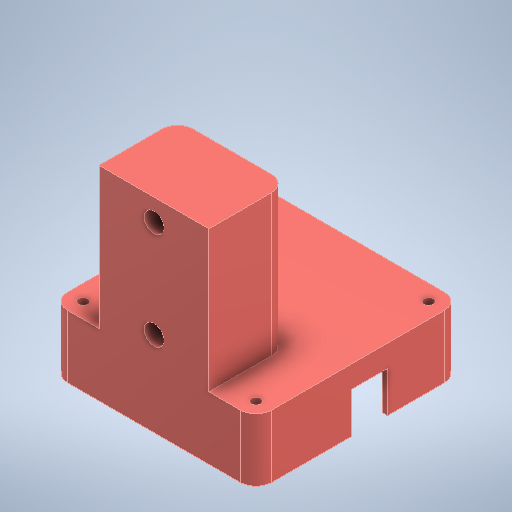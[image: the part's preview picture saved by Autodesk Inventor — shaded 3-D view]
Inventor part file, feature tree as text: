
AUTODESK INVENTOR PART (.ipt)
format: ipt  version: 2025.2 (Build 292293000, 293)  size: 555,008 bytes
history: native  units: in
note: dims shown in document units (in); Inventor stores cm internally (conversion verified against a paired STEP export)
features: extrude x18, sketch x18, fillet x7, other x5, direct_edit x2, projected_geometry x1
ambient origin geometry x8: Origin, YZ Plane, XZ Plane, XY Plane, X Axis, Y Axis, Z Axis, Center Point
bodies: Solid1 (feature_tree)
feature tree (51):
  direct_edit  "Direct Edit1"
  extrude  "Extrusion1"  Depth=0.4331in
  fillet  "Fillet1"  Radius=0.3543in
  fillet  "Fillet2"  Radius=0.4331in
  extrude  "Extrusion2"  Depth=0.1575in
  extrude  "Extrusion3"  Depth=0.1575in
  direct_edit  "Direct Edit2"
  extrude  "Extrusion4"  Depth=0.1667in
  extrude  "Extrusion5"  Depth=0.1575in TaperAngle=0.0deg
  extrude  "Extrusion6"  Depth=0.1575in TaperAngle=0.0deg
  extrude  "Extrusion7"  Depth=1.0812in TaperAngle=0.0deg
  extrude  "Extrusion8"  Depth=0.2938in TaperAngle=0.0deg
  extrude  "Extrusion9"  Depth=0.0787in TaperAngle=0.0deg
  extrude  "Extrusion10"  Depth=0.0787in TaperAngle=0.0deg
  extrude  "Extrusion11"  Depth=0.0787in TaperAngle=0.0deg
  extrude  "Extrusion12"  Depth=0.0787in TaperAngle=0.0deg
  extrude  "Extrusion13"  Depth=0.9843in
  extrude  "Extrusion14"  Depth=0.3937in
  extrude  "Extrusion15"  Depth=1.7717in
  extrude  "Extrusion16"  Depth=0.2756in
  extrude  "Extrusion17"  Depth=0.2756in
  extrude  "Extrusion18"  Depth=0.3937in
  fillet  "Fillet3"  Radius=0.3937in
  fillet  "Fillet4"  Radius=0.2165in
  fillet  "Fillet5"  Radius=0.1969in
  fillet  "Fillet6"  Radius=0.1969in
  fillet  "Fillet7"  Radius=0.1969in
  sketch  "Sketch1"  dims[d0=0.3543in d1=0.4331in d2=0.3543in d3=0.4331in]
  sketch  "Sketch2"  dims[d4=0.1575in d5=0.0in d6=0.1575in]
  sketch  "Sketch3"  dims[d7=0.1575in d8=1.0885in]
  projected_geometry  "Projected Loop1"
  sketch  "Sketch4"  dims[d9=0.1667in d10=0.1667in]
  sketch  "Sketch5"  dims[d11=1.0866in d12=0.1575in d13=0.0in]
  sketch  "Sketch6"  dims[d14=0.1667in d15=0.1575in d16=0.0in]
  sketch  "Sketch7"  dims[d17=0.8563in d18=0.0in d19=1.0812in d20=0.0in]
  sketch  "Sketch8"  dims[d21=0.3312in d22=0.0in d23=0.2938in d24=0.0in]
  sketch  "Sketch9"  dims[d25=0.0787in d26=0.0in d27=0.0787in d28=0.0in]
  sketch  "Sketch10"  dims[d29=0.0787in d30=0.0in d31=0.0787in d32=0.0in]
  sketch  "Sketch11"  dims[d33=0.0787in d34=0.0in d35=0.0787in d36=0.0in]
  sketch  "Sketch12"  dims[d37=0.0787in d38=0.0in d39=0.0787in d40=0.0in]
  sketch  "Sketch13"  dims[d41=1.378in d42=0.9843in]
  sketch  "Sketch14"  dims[d43=0.3937in d44=0.3937in]
  sketch  "Sketch15"  dims[d45=1.7717in d46=0.0in d47=0.2441in]
  sketch  "Sketch16"  dims[d48=0.689in d49=0.2756in]
  sketch  "Sketch17"  dims[d50=0.2441in d51=0.2756in]
  sketch  "Sketch18"  dims[d52=0.9843in d53=0.0in d54=0.3937in d55=0.3937in d56=0.2165in d57=0.0in d58=0.1969in d59=0.1969in d60=0.1969in d61=0.1969in d62=0.1969in]
  other  "Com_Top_A"
  other  "Delete1"
  other  "Delete2"
  other  "Delete3"
  other  "Delete4"
